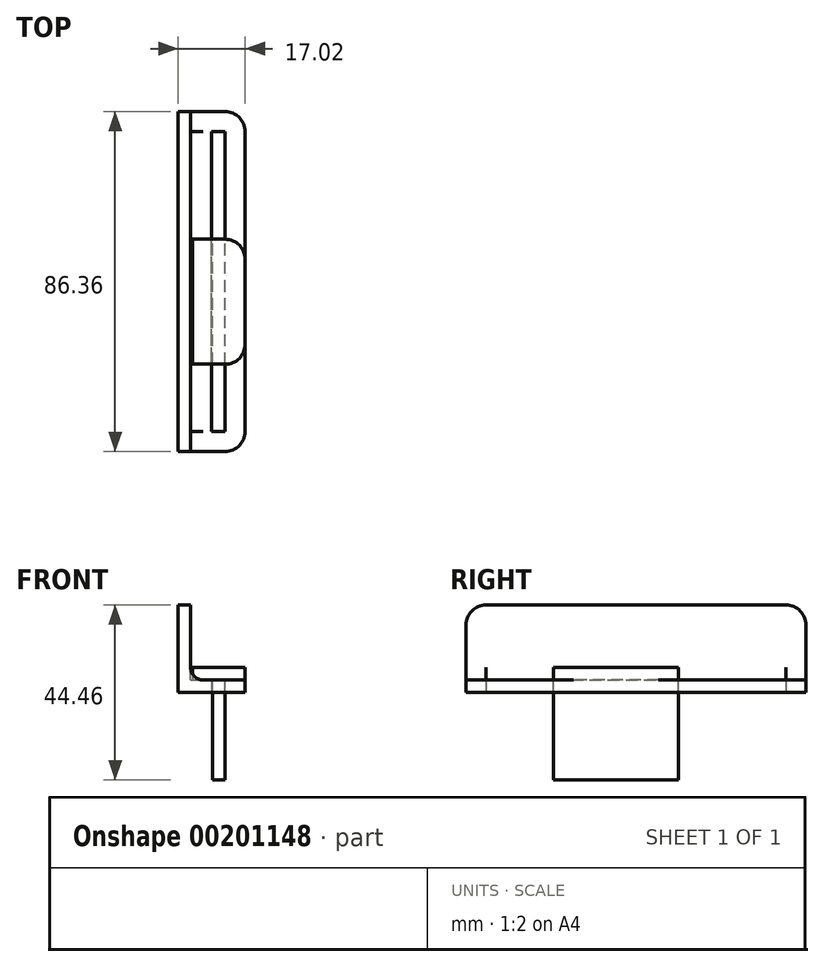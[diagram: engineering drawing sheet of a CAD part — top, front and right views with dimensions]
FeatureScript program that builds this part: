
annotation { "Feature Type Name" : "Feature", "Feature Type Description" : "" }
export const myFeature = defineFeature(function(context is Context, id is Id, definition is map)
    precondition{}
    {
        {
            var Q0;
            Q0=qCreatedBy(makeId("Top.planeOp"),FACE);
            var sketch = newSketch(context, id + "F0", { "sketchPlane" : qUnion([Q0])});
            skLineSegment(sketch, "E0.bottom", {"start": v(0, 0) * mm, "end": v(3.43, 0) * mm});
            skLineSegment(sketch, "E0.top", {"start": v(0, 76.2) * mm, "end": v(3.43, 76.2) * mm});
            skLineSegment(sketch, "E0.left", {"start": v(0, 0) * mm, "end": v(0, 76.2) * mm});
            skLineSegment(sketch, "E0.right", {"start": v(3.43, 0) * mm, "end": v(3.43, 76.2) * mm});
            skPoint(sketch, "E1.positionSnap0", {"position": v(0, 38.1) * mm});
            skPoint(sketch, "E1.positionSnap1", {"position": v(1.71, 0) * mm});
            skLineSegment(sketch, "E2.bottom", {"start": v(8.5, 81.28) * mm, "end": v(-8.5, 81.28) * mm});
            skLineSegment(sketch, "E2.top", {"start": v(8.5, -5.08) * mm, "end": v(-8.5, -5.08) * mm});
            skLineSegment(sketch, "E2.left", {"start": v(8.5, 81.28) * mm, "end": v(8.5, -5.08) * mm});
            skLineSegment(sketch, "E2.right", {"start": v(-8.5, 81.28) * mm, "end": v(-8.5, -5.08) * mm});
            skSolve(sketch);
        }
        {
            var Q0;
            Q0=makeQuery(id+"F0.imprint","IMPRINT",FACE,{"disambiguationData":[TD([[makeQuery(id+"F0.imprint","IMPRINT",EDGE,{"derivedFrom":sQuery(id+"F0.wireOp",EDGE,"E0.bottom")}),-1.0]])]});
            extrude(context, id + "F1", {"entities" : qUnion([Q0]), "depth" : 3.17 * mm});
        }
        {
            var Q0;
            Q0=makeQuery(id+"F1.opExtrude","CAP_FACE",FACE,{"disambiguationData":[OSD([sQuery(id+"F0.wireOp",EDGE,"E0.bottom"),sQuery(id+"F0.wireOp",EDGE,"E0.top"),sQuery(id+"F0.wireOp",EDGE,"E0.left"),sQuery(id+"F0.wireOp",EDGE,"E0.right"),sQuery(id+"F0.wireOp",EDGE,"E2.bottom"),sQuery(id+"F0.wireOp",EDGE,"E2.top"),sQuery(id+"F0.wireOp",EDGE,"E2.left"),sQuery(id+"F0.wireOp",EDGE,"E2.right")])],"isStart":false});
            var sketch = newSketch(context, id + "F2", { "sketchPlane" : qUnion([Q0])});
            skLineSegment(sketch, "E3.bottom", {"start": v(-8.5, 81.28) * mm, "end": v(-5.33, 81.28) * mm});
            skLineSegment(sketch, "E3.top", {"start": v(-8.5, -5.08) * mm, "end": v(-5.33, -5.08) * mm});
            skLineSegment(sketch, "E3.left", {"start": v(-8.5, 81.28) * mm, "end": v(-8.5, -5.08) * mm});
            skLineSegment(sketch, "E3.right", {"start": v(-5.33, 81.28) * mm, "end": v(-5.33, -5.08) * mm});
            skSolve(sketch);
        }
        {
            var Q0;
            Q0 = qSketchRegion(id + "F2", true);
            extrude(context, id + "F3", {"entities" : qUnion([Q0]), "operationType" : NewBodyOperationType.ADD, "depth" : 19.05 * mm});
        }
        {
            var Q0;
            Q0=makeQuery(id+"F1.opExtrude","CAP_FACE",FACE,{"disambiguationData":[OSD([sQuery(id+"F0.wireOp",EDGE,"E0.bottom"),sQuery(id+"F0.wireOp",EDGE,"E0.top"),sQuery(id+"F0.wireOp",EDGE,"E0.left"),sQuery(id+"F0.wireOp",EDGE,"E0.right"),sQuery(id+"F0.wireOp",EDGE,"E2.bottom"),sQuery(id+"F0.wireOp",EDGE,"E2.top"),sQuery(id+"F0.wireOp",EDGE,"E2.left"),sQuery(id+"F0.wireOp",EDGE,"E2.right")])],"isStart":false});
            var sketch = newSketch(context, id + "F4", { "sketchPlane" : qUnion([Q0])});
            skLineSegment(sketch, "E4.bottom", {"start": v(8.5, 17.1) * mm, "end": v(-4.83, 17.1) * mm});
            skLineSegment(sketch, "E4.top", {"start": v(8.5, 48.85) * mm, "end": v(-4.83, 48.85) * mm});
            skLineSegment(sketch, "E4.left", {"start": v(8.5, 17.1) * mm, "end": v(8.5, 48.85) * mm});
            skLineSegment(sketch, "E4.right", {"start": v(-4.83, 17.1) * mm, "end": v(-4.83, 48.85) * mm});
            skSolve(sketch);
        }
        {
            var Q0;
            Q0 = qSketchRegion(id + "F4", true);
            extrude(context, id + "F5", {"entities" : qUnion([Q0]), "depth" : 3.17 * mm});
        }
        {
            var Q0;
            Q0=makeQuery(id+"F5.opExtrude","CAP_FACE",FACE,{"disambiguationData":[OSD([sQuery(id+"F4.wireOp",EDGE,"E4.bottom"),sQuery(id+"F4.wireOp",EDGE,"E4.top"),sQuery(id+"F4.wireOp",EDGE,"E4.left"),sQuery(id+"F4.wireOp",EDGE,"E4.right")])],"isStart":true});
            var sketch = newSketch(context, id + "F6", { "sketchPlane" : qUnion([Q0])});
            skLineSegment(sketch, "E5.bottom", {"start": v(0.25, -17.1) * mm, "end": v(3.43, -17.1) * mm});
            skLineSegment(sketch, "E5.top", {"start": v(0.25, -48.85) * mm, "end": v(3.43, -48.85) * mm});
            skLineSegment(sketch, "E5.left", {"start": v(0.25, -17.1) * mm, "end": v(0.25, -48.85) * mm});
            skLineSegment(sketch, "E5.right", {"start": v(3.43, -17.1) * mm, "end": v(3.43, -48.85) * mm});
            skSolve(sketch);
        }
        {
            var Q0;
            Q0=makeQuery(id+"F6.imprint","IMPRINT",FACE,{"disambiguationData":[TD([[makeQuery(id+"F6.imprint","IMPRINT",EDGE,{"derivedFrom":sQuery(id+"F6.wireOp",EDGE,"E5.bottom")}),1.0]])]});
            extrude(context, id + "F7", {"entities" : qUnion([Q0]), "operationType" : NewBodyOperationType.ADD, "depth" : 25.4 * mm});
        }
        {
            var Q0;
            Q0=makeQuery(id+"F5.opExtrude","SWEPT_EDGE",EDGE,{"disambiguationData":[OSD([sQuery(id+"F0.wireOp",EDGE,"E2.left"),sQuery(id+"F4.wireOp",EDGE,"E4.bottom"),sQuery(id+"F4.wireOp",EDGE,"E4.left")])]});
            var Q1;
            Q1=makeQuery(id+"F5.opExtrude","SWEPT_EDGE",EDGE,{"disambiguationData":[OSD([sQuery(id+"F0.wireOp",EDGE,"E2.left"),sQuery(id+"F4.wireOp",EDGE,"E4.top"),sQuery(id+"F4.wireOp",EDGE,"E4.left")])]});
            var Q2;
            Q2=makeQuery(id+"F1.opExtrude","SWEPT_EDGE",EDGE,{"disambiguationData":[OSD([sQuery(id+"F0.wireOp",EDGE,"E2.top"),sQuery(id+"F0.wireOp",EDGE,"E2.left")])]});
            var Q3;
            Q3=makeQuery(id+"F1.opExtrude","SWEPT_EDGE",EDGE,{"disambiguationData":[OSD([sQuery(id+"F0.wireOp",EDGE,"E2.bottom"),sQuery(id+"F0.wireOp",EDGE,"E2.left")])]});
            var Q4;
            Q4=makeQuery(id+"F3.opExtrude","CAP_EDGE",EDGE,{"disambiguationData":[OSD([sQuery(id+"F2.wireOp",EDGE,"E3.top")])],"isStart":false});
            var Q5;
            Q5=makeQuery(id+"F3.opExtrude","CAP_EDGE",EDGE,{"disambiguationData":[OSD([sQuery(id+"F2.wireOp",EDGE,"E3.bottom")])],"isStart":false});
            fillet(context, id + "F8", {"entities" : qUnion([Q0, Q1, Q2, Q3, Q4, Q5]), "radius" : 5.08 * mm, "tangentPropagation" : true, "allowEdgeOverflow" : false});
        }
        {
            var Q0;
            Q0=makeQuery(id+"F3.boolean.opBoolean","MERGE",FACE,{"derivedFrom":[makeQuery(id+"F1.opExtrude","SWEPT_FACE",FACE,{"disambiguationData":[OSD([sQuery(id+"F0.wireOp",EDGE,"E2.top")])]}),makeQuery(id+"F3.opExtrude","SWEPT_FACE",FACE,{"disambiguationData":[OSD([sQuery(id+"F2.wireOp",EDGE,"E3.top")])]})]});
            var sketch = newSketch(context, id + "F9", { "sketchPlane" : qUnion([Q0])});
            skLineSegment(sketch, "E6.bottom", {"start": v(-5.33, 3.18) * mm, "end": v(-2.16, 3.18) * mm});
            skLineSegment(sketch, "E6.left", {"start": v(-5.33, 3.18) * mm, "end": v(-5.33, 6.35) * mm});
            skArc(sketch, "E7", {"start": v(-5.33, 6.35) * mm, "mid": v(-4.4, 4.1) * mm, "end": v(-2.16, 3.18) * mm});
            skSolve(sketch);
        }
        {
            var Q0;
            Q0=makeQuery(id+"F3.boolean.opBoolean","MERGE",FACE,{"derivedFrom":[makeQuery(id+"F1.opExtrude","SWEPT_FACE",FACE,{"disambiguationData":[OSD([sQuery(id+"F0.wireOp",EDGE,"E2.bottom")])]}),makeQuery(id+"F3.opExtrude","SWEPT_FACE",FACE,{"disambiguationData":[OSD([sQuery(id+"F2.wireOp",EDGE,"E3.bottom")])]})]});
            var sketch = newSketch(context, id + "F10", { "sketchPlane" : qUnion([Q0])});
            skArc(sketch, "E8.0", {"start": v(5.33, 6.35) * mm, "mid": v(4.4, 4.1) * mm, "end": v(2.16, 3.18) * mm});
            skLineSegment(sketch, "E9.0", {"start": v(5.33, 3.18) * mm, "end": v(5.33, 6.35) * mm});
            skLineSegment(sketch, "E10.0", {"start": v(5.33, 3.18) * mm, "end": v(2.16, 3.18) * mm});
            skSolve(sketch);
        }
        {
            var Q0;
            Q0 = qSketchRegion(id + "F9", true);
            var Q1;
            Q1=makeQuery(id+"F1.opExtrude","SWEPT_FACE",FACE,{"disambiguationData":[OSD([sQuery(id+"F0.wireOp",EDGE,"E0.bottom")])]});
            extrude(context, id + "F11", {"entities" : qUnion([Q0]), "operationType" : NewBodyOperationType.ADD, "endBound" : BoundingType.UP_TO_SURFACE, "oppositeDirection" : true, "endBoundEntityFace" : qUnion([Q1]), "depth" : 5.08 * mm});
        }
        {
            var Q0;
            Q0 = qSketchRegion(id + "F10", true);
            var Q1;
            Q1=makeQuery(id+"F1.opExtrude","SWEPT_FACE",FACE,{"disambiguationData":[OSD([sQuery(id+"F0.wireOp",EDGE,"E0.top")])]});
            extrude(context, id + "F12", {"entities" : qUnion([Q0]), "operationType" : NewBodyOperationType.ADD, "endBound" : BoundingType.UP_TO_SURFACE, "oppositeDirection" : true, "endBoundEntityFace" : qUnion([Q1]), "depth" : 25.4 * mm});
        }
    });
